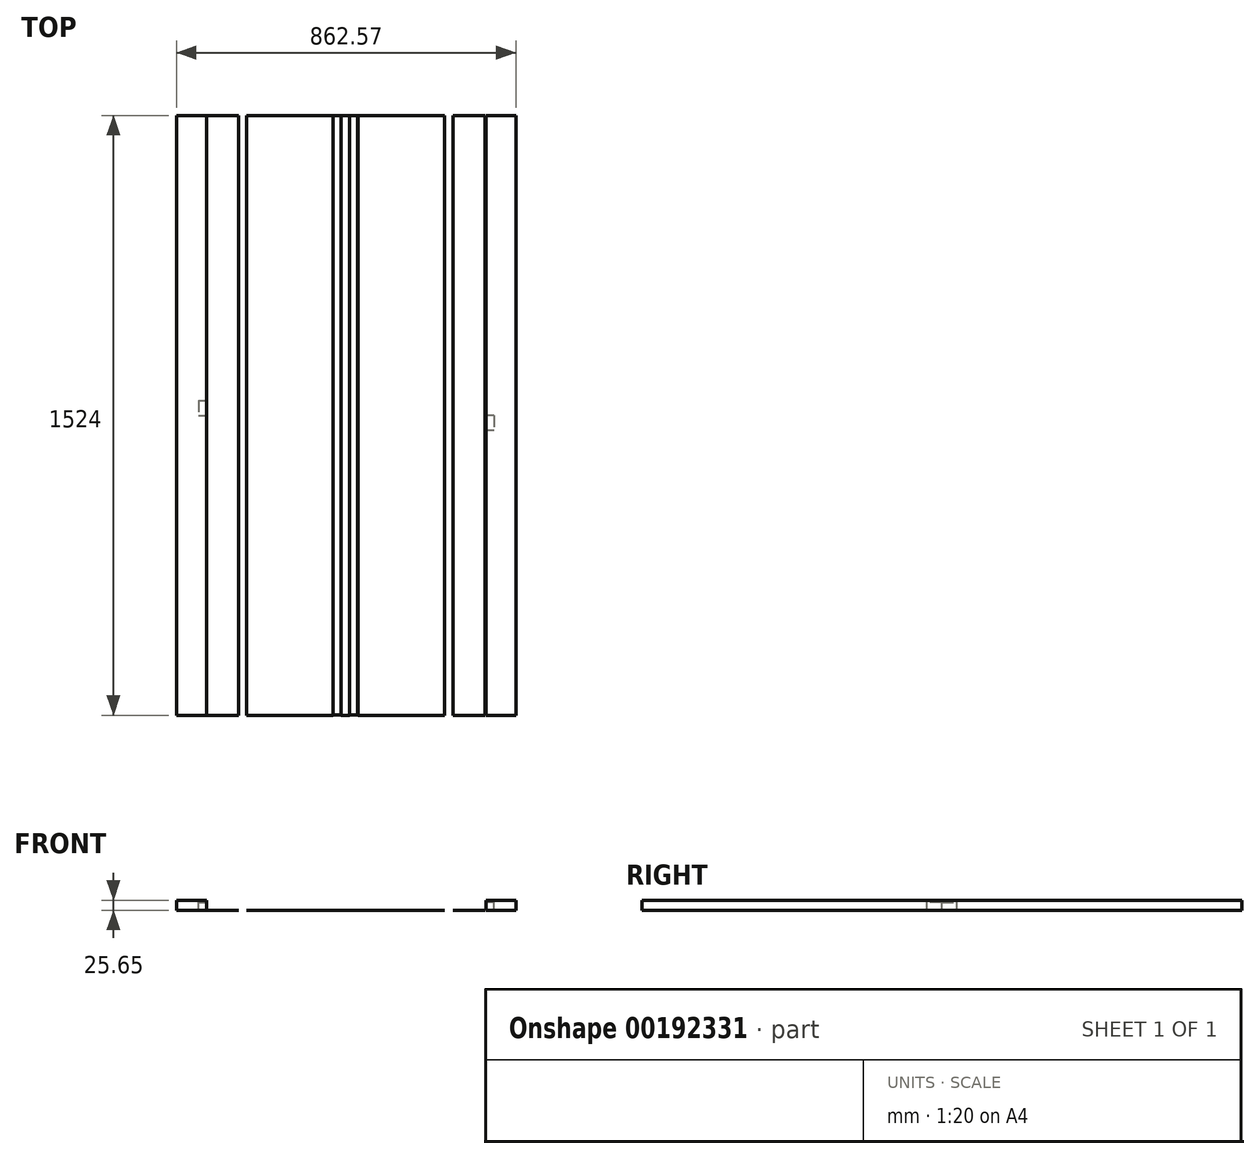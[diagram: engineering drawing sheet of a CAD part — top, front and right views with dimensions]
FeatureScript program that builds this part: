
annotation { "Feature Type Name" : "Feature", "Feature Type Description" : "" }
export const myFeature = defineFeature(function(context is Context, id is Id, definition is map)
    precondition{}
    {
        {
            var Q0;
            Q0=qCreatedBy(makeId("Top.planeOp"),FACE);
            var sketch = newSketch(context, id + "F0", { "sketchPlane" : qUnion([Q0])});
            skLineSegment(sketch, "E0.bottom", {"start": v(-219.7, 0) * mm, "end": v(0, 0) * mm});
            skLineSegment(sketch, "E0.top", {"start": v(-219.7, -1524) * mm, "end": v(0, -1524) * mm});
            skLineSegment(sketch, "E0.left", {"start": v(-219.7, 0) * mm, "end": v(-219.7, -1524) * mm});
            skLineSegment(sketch, "E0.right", {"start": v(0, 0) * mm, "end": v(0, -1524) * mm});
            skLineSegment(sketch, "E1.bottom", {"start": v(-502.45, 0) * mm, "end": v(-282.74, 0) * mm});
            skLineSegment(sketch, "E1.top", {"start": v(-502.45, -1524) * mm, "end": v(-282.74, -1524) * mm});
            skLineSegment(sketch, "E1.left", {"start": v(-502.45, 0) * mm, "end": v(-502.45, -1524) * mm});
            skLineSegment(sketch, "E1.right", {"start": v(-282.74, 0) * mm, "end": v(-282.74, -1524) * mm});
            skSolve(sketch);
        }
        {
            var Q0;
            Q0=qCreatedBy(makeId("Top.planeOp"),FACE);
            var sketch = newSketch(context, id + "F1", { "sketchPlane" : qUnion([Q0])});
            skLineSegment(sketch, "E2.top", {"start": v(0, -1524) * mm, "end": v(20.32, -1524) * mm});
            skLineSegment(sketch, "E2.left", {"start": v(0, 0) * mm, "end": v(0, -1524) * mm});
            skLineSegment(sketch, "E2.right", {"start": v(20.32, 0) * mm, "end": v(20.32, -1524) * mm});
            skLineSegment(sketch, "E3.bottom", {"start": v(-522.67, 0) * mm, "end": v(-603.95, 0) * mm});
            skLineSegment(sketch, "E3.top", {"start": v(-522.67, -1524) * mm, "end": v(-603.95, -1524) * mm});
            skLineSegment(sketch, "E3.left", {"start": v(-522.67, 0) * mm, "end": v(-522.67, -1524) * mm});
            skLineSegment(sketch, "E3.right", {"start": v(-603.95, 0) * mm, "end": v(-603.95, -1524) * mm});
            skSolve(sketch);
        }
        {
            var Q0;
            Q0=qCreatedBy(makeId("Top.planeOp"),FACE);
            var sketch = newSketch(context, id + "F2", { "sketchPlane" : qUnion([Q0])});
            skLineSegment(sketch, "E4.bottom", {"start": v(105.67, 0) * mm, "end": v(181.87, 0) * mm});
            skLineSegment(sketch, "E4.top", {"start": v(105.67, -1524) * mm, "end": v(181.87, -1524) * mm});
            skLineSegment(sketch, "E4.left", {"start": v(105.67, 0) * mm, "end": v(105.67, -1524) * mm});
            skLineSegment(sketch, "E4.right", {"start": v(181.87, 0) * mm, "end": v(181.87, -1524) * mm});
            skLineSegment(sketch, "E5.bottom", {"start": v(-604.5, 0) * mm, "end": v(-680.7, 0) * mm});
            skLineSegment(sketch, "E5.top", {"start": v(-604.5, -1524) * mm, "end": v(-680.7, -1524) * mm});
            skLineSegment(sketch, "E5.left", {"start": v(-604.5, 0) * mm, "end": v(-604.5, -1524) * mm});
            skLineSegment(sketch, "E5.right", {"start": v(-680.7, 0) * mm, "end": v(-680.7, -1524) * mm});
            skSolve(sketch);
        }
        {
            var Q0;
            Q0 = qSketchRegion(id + "F2", true);
            extrude(context, id + "F3", {"entities" : qUnion([Q0]), "depth" : 25.4 * mm});
        }
        {
            var Q0;
            Q0=makeQuery(id+"F3.opExtrude","SWEPT_FACE",FACE,{"disambiguationData":[OSD([sQuery(id+"F2.wireOp",EDGE,"E5.left")])]});
            var sketch = newSketch(context, id + "F4", { "sketchPlane" : qUnion([Q0])});
            skLineSegment(sketch, "E6.bottom", {"start": v(-762, 0) * mm, "end": v(-723.9, 0) * mm});
            skLineSegment(sketch, "E6.top", {"start": v(-762, 20.32) * mm, "end": v(-723.9, 20.32) * mm});
            skLineSegment(sketch, "E6.left", {"start": v(-762, 0) * mm, "end": v(-762, 20.32) * mm});
            skLineSegment(sketch, "E6.right", {"start": v(-723.9, 0) * mm, "end": v(-723.9, 20.32) * mm});
            skSolve(sketch);
        }
        {
            var Q0;
            Q0 = qSketchRegion(id + "F4", true);
            extrude(context, id + "F5", {"entities" : qUnion([Q0]), "operationType" : NewBodyOperationType.REMOVE, "oppositeDirection" : true, "depth" : 20.32 * mm});
        }
        {
            var Q0;
            Q0=makeQuery(id+"F3.opExtrude","SWEPT_FACE",FACE,{"disambiguationData":[OSD([sQuery(id+"F2.wireOp",EDGE,"E4.left")])]});
            var sketch = newSketch(context, id + "F6", { "sketchPlane" : qUnion([Q0])});
            skLineSegment(sketch, "E7.bottom", {"start": v(762, 0) * mm, "end": v(800.1, 0) * mm});
            skLineSegment(sketch, "E7.top", {"start": v(762, 20.32) * mm, "end": v(800.1, 20.32) * mm});
            skLineSegment(sketch, "E7.left", {"start": v(762, 0) * mm, "end": v(762, 20.32) * mm});
            skLineSegment(sketch, "E7.right", {"start": v(800.1, 0) * mm, "end": v(800.1, 20.32) * mm});
            skSolve(sketch);
        }
        {
            var Q0;
            Q0 = qSketchRegion(id + "F6", true);
            extrude(context, id + "F7", {"entities" : qUnion([Q0]), "operationType" : NewBodyOperationType.REMOVE, "oppositeDirection" : true, "depth" : 20.32 * mm});
        }
        {
            var Q0;
            Q0 = qSketchRegion(id + "F0", true);
            extrude(context, id + "F8", {"entities" : qUnion([Q0]), "oppositeDirection" : true, "depth" : 0.25 * mm});
        }
        {
            var Q0;
            Q0 = qSketchRegion(id + "F1", true);
            extrude(context, id + "F9", {"entities" : qUnion([Q0]), "oppositeDirection" : true, "depth" : 0.25 * mm});
        }
        {
            var Q0;
            Q0=qCreatedBy(makeId("Top.planeOp"),FACE);
            var sketch = newSketch(context, id + "F10", { "sketchPlane" : qUnion([Q0])});
            skLineSegment(sketch, "E8.bottom", {"start": v(21.92, 0) * mm, "end": v(103.2, 0) * mm});
            skLineSegment(sketch, "E8.top", {"start": v(21.92, -1524) * mm, "end": v(103.2, -1524) * mm});
            skLineSegment(sketch, "E8.left", {"start": v(21.92, 0) * mm, "end": v(21.92, -1524) * mm});
            skLineSegment(sketch, "E8.right", {"start": v(103.2, 0) * mm, "end": v(103.2, -1524) * mm});
            skSolve(sketch);
        }
        {
            var Q0;
            Q0 = qSketchRegion(id + "F10", true);
            extrude(context, id + "F11", {"entities" : qUnion([Q0]), "operationType" : NewBodyOperationType.ADD, "depth" : 0.25 * mm});
        }
        {
            var Q0;
            Q0=qCreatedBy(makeId("Top.planeOp"),FACE);
            var sketch = newSketch(context, id + "F12", { "sketchPlane" : qUnion([Q0])});
            skLineSegment(sketch, "E9", {"start": v(-241.05, 0) * mm, "end": v(-241.05, -1522.6) * mm});
            skLineSegment(sketch, "E10", {"start": v(-241.05, -1522.6) * mm, "end": v(-262.44, -1522.6) * mm});
            skLineSegment(sketch, "E11", {"start": v(-262.44, -1522.6) * mm, "end": v(-282.76, -1522.6) * mm});
            skLineSegment(sketch, "E12", {"start": v(-282.76, -1522.6) * mm, "end": v(-282.76, 0) * mm});
            skLineSegment(sketch, "E13", {"start": v(-282.76, 0) * mm, "end": v(-262.44, 0) * mm});
            skLineSegment(sketch, "E14", {"start": v(-262.44, 0) * mm, "end": v(-262.44, -1522.6) * mm});
            skLineSegment(sketch, "E15", {"start": v(-284.48, -1522.6) * mm, "end": v(-282.76, -1522.6) * mm});
            skLineSegment(sketch, "E16", {"start": v(-282.76, 0) * mm, "end": v(-284.48, 0) * mm});
            skLineSegment(sketch, "E17", {"start": v(-262.44, 0) * mm, "end": v(-241.05, 0) * mm});
            skLineSegment(sketch, "E18", {"start": v(-241.05, 0) * mm, "end": v(-220.73, 0) * mm});
            skLineSegment(sketch, "E19", {"start": v(-220.73, 0) * mm, "end": v(-220.73, -1522.6) * mm});
            skLineSegment(sketch, "E20", {"start": v(-220.73, -1522.6) * mm, "end": v(-241.05, -1522.6) * mm});
            skSolve(sketch);
        }
        {
            var Q0;
            Q0=makeQuery(id+"F12.imprint","IMPRINT",FACE,{"disambiguationData":[TD([[makeQuery(id+"F12.imprint","IMPRINT",EDGE,{"derivedFrom":sQuery(id+"F12.wireOp",EDGE,"E11")}),-1.0]])]});
            var Q1;
            Q1=makeQuery(id+"F12.imprint","IMPRINT",FACE,{"disambiguationData":[TD([[makeQuery(id+"F12.imprint","IMPRINT",EDGE,{"derivedFrom":sQuery(id+"F12.wireOp",EDGE,"E9")}),1.0]])]});
            extrude(context, id + "F13", {"entities" : qUnion([Q0, Q1]), "operationType" : NewBodyOperationType.ADD, "depth" : 0.25 * mm});
        }
        {
            var Q0;
            Q0=qCreatedBy(makeId("Top.planeOp"),FACE);
            var sketch = newSketch(context, id + "F14", { "sketchPlane" : qUnion([Q0])});
            skLineSegment(sketch, "E21.bottom", {"start": v(-262.1, 0) * mm, "end": v(-241.27, 0) * mm});
            skLineSegment(sketch, "E21.top", {"start": v(-262.1, -1524) * mm, "end": v(-241.27, -1524) * mm});
            skLineSegment(sketch, "E21.left", {"start": v(-262.1, 0) * mm, "end": v(-262.1, -1524) * mm});
            skLineSegment(sketch, "E21.right", {"start": v(-241.27, 0) * mm, "end": v(-241.27, -1524) * mm});
            skSolve(sketch);
        }
        {
            var Q0;
            Q0 = qSketchRegion(id + "F14", true);
            extrude(context, id + "F15", {"entities" : qUnion([Q0]), "depth" : 0.25 * mm});
        }
    });
